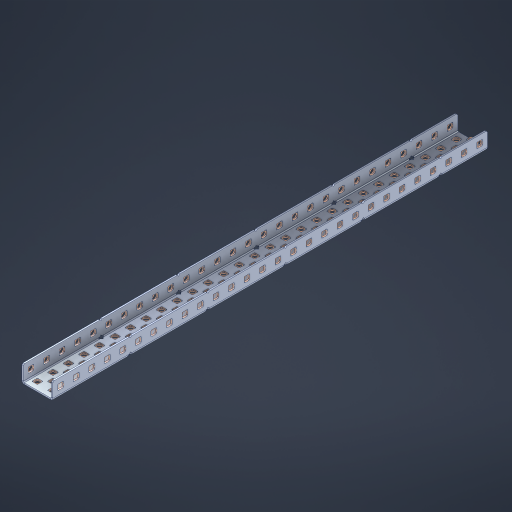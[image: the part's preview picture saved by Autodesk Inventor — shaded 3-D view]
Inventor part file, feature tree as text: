
AUTODESK INVENTOR PART (.ipt)
format: ipt  version: 2023 (Build 270158000, 158)  size: 1,764,864 bytes
history: native  units: in
note: dims shown in document units (in); Inventor stores cm internally (conversion verified against a paired STEP export)
features: other x147, extrude x138, sheet_metal_op x11, sketch x10, pattern_linear x2, mirror x1, chamfer x1
ambient origin geometry x8: Origin, YZ Plane, XZ Plane, XY Plane, X Axis, Y Axis, Z Axis, Center Point
bodies: Solid1 (feature_tree), Body (feature_tree)
feature tree (310):
  sheet_metal_op  "Flanges"
  other  "Flange Pattern Plane"
  other  "Flange Pattern Sketch"
  sheet_metal_op  "Flange Pattern"
  sheet_metal_op  "Body Pattern"
  pattern_linear  "Center Pattern"  Spacing1=0.0469in  [1 undecoded]
  other  "Arc Length"
  mirror  "Notch Mirror"
  pattern_linear  "Notch Pattern"  Spacing1=0.182in  [1 undecoded]
  chamfer  "End Chamfer"
  extrude  "Half Cut"  Depth=0.02in
  sketch  "Sketch1"  dims[d0=1.0in]
  other  "Plate1"
  sketch  "Sketch2"  dims[d1=14.0in]
  other  "Plate2"
  sheet_metal_op  "Bend1"
  sheet_metal_op  "Corner1"
  sketch  "Sketch3"  dims[d2=0.0469in]
  sketch  "Sketch7"  dims[d3=0.0469in]
  other  "Srf1"
  other  "Srf2"
  sketch  "Sketch8"  dims[d4=0.0234in]
  sketch  "Sketch9"  dims[d5=0.0938in]
  other  "Srf91"
  sheet_metal_op  "Body Pattern Sketch"
  other  "Srf92"
  sketch  "Sketch13"  dims[d6=0.0469in]
  sketch  "Sketch14"  dims[d7=0.5in d8=90.0deg d9=0.0312in]
  sketch  "Sketch15"  dims[d10=0.1875in]
  sketch  "Sketch16"  dims[d11=0.0469in d12=0.0469in d16=0.182in d17=0.02in d18=0.0469in d19=0.0in d20=0.25in d21=0.25in d38=11.0236in d40=0.5in d41=0.7874in d43=1.0in d46=0.172in d47=1.0in d48=0.0in d49=0.182in d50=0.02in d51=0.25in d52=0.25in d53=0.0469in d54=0.0in d55=0.172in d56=1.0in d57=0.0in d58=0.25in d60=11.0236in d62=0.5in d63=0.7874in d65=0.5in d85=0.1227in d86=0.1659in d88=0.04in d89=0.0469in d90=0.0in d91=0.04in d92=0.0491in d95=2.5in d96=0.04in d97=0.25in d98=45.0deg d99=0.25in d100=0.5in d101=0.0in d102=2.497in d106=0.182in d107=0.02in d108=0.5in d109=0.5in d110=0.0469in d111=0.0in d112=0.172in d113=0.5in d114=0.0in d117=0.5in d118=0.5in d119=0.5in]
  other  "Srf786"
  other  "Srf823"
  other  "Srf824"
  other  "Srf825"
  other  "Srf826"
  other  "Srf827"
  other  "Srf828"
  other  "Srf829"
  other  "Srf856"
  other  "Srf857"
  other  "Srf858"
  other  "Srf859"
  other  "Srf860"
  other  "Srf861"
  other  "Srf862"
  other  "Srf889"
  other  "Srf890"
  other  "Srf891"
  other  "Srf892"
  other  "Srf893"
  other  "Srf894"
  other  "Srf895"
  other  "Srf896"
  other  "Srf922"
  other  "Srf923"
  other  "Srf924"
  other  "Srf925"
  other  "Srf926"
  other  "Srf959"
  other  "Srf960"
  other  "Srf961"
  other  "Srf962"
  other  "Srf963"
  other  "Srf996"
  other  "Srf997"
  other  "Srf998"
  other  "Srf999"
  other  "Srf1000"
  other  "Srf1143"
  other  "Srf1144"
  other  "Srf1145"
  other  "Srf1146"
  other  "Srf1147"
  other  "Srf1148"
  other  "Srf1149"
  other  "Srf1150"
  other  "Srf1151"
  other  "Srf1152"
  other  "Srf1153"
  other  "Srf1154"
  other  "Srf1155"
  other  "Srf1156"
  other  "Srf1157"
  other  "Srf1158"
  other  "Srf1159"
  other  "Srf1160"
  other  "Srf1161"
  other  "Srf1162"
  other  "Srf1163"
  other  "Srf1164"
  other  "Srf1165"
  other  "Srf1166"
  other  "Srf1167"
  other  "Srf1168"
  other  "Srf1169"
  other  "Srf1170"
  other  "Srf1171"
  other  "Srf1172"
  other  "Srf1173"
  other  "Srf1174"
  other  "Srf1175"
  other  "Srf1176"
  other  "Srf1177"
  other  "Srf1178"
  other  "Srf1179"
  other  "Srf1180"
  other  "Srf1181"
  other  "Srf1182"
  other  "Srf1183"
  other  "Srf1184"
  other  "Srf1199"
  other  "Srf1200"
  other  "Srf1201"
  other  "Srf1202"
  other  "Srf1203"
  other  "Srf1204"
  other  "Srf1205"
  other  "Srf1206"
  other  "Srf1207"
  other  "Srf1208"
  other  "Srf1209"
  other  "Srf1210"
  other  "Srf1211"
  other  "Srf1212"
  other  "Srf1213"
  other  "Srf1214"
  other  "Srf1215"
  other  "Srf1216"
  other  "Srf1217"
  other  "Srf1218"
  other  "Srf1219"
  other  "Srf1220"
  other  "Srf1221"
  other  "Srf1222"
  other  "Srf1223"
  other  "Srf1224"
  other  "Srf1225"
  other  "Srf1226"
  other  "Srf1227"
  other  "Srf1228"
  other  "Srf1229"
  other  "Srf1230"
  other  "Srf1231"
  other  "Srf1232"
  other  "Srf1233"
  other  "Srf1234"
  other  "Srf1235"
  other  "Srf1236"
  other  "Srf1237"
  other  "Srf1238"
  other  "Srf1239"
  other  "Srf1240"
  other  "Srf1255"
  other  "Srf1256"
  other  "Srf1257"
  other  "Srf1258"
  other  "Srf1259"
  other  "Srf1260"
  other  "Srf1261"
  other  "Srf1262"
  other  "Srf1263"
  other  "Srf1264"
  other  "Srf1265"
  other  "Srf1266"
  other  "Srf1267"
  other  "Srf1268"
  sheet_metal_op  "Flange Stamp"
  sheet_metal_op  "Flange Circle"
  sheet_metal_op  "Body Stamp"
  sheet_metal_op  "Body Circle"
  other  "Center Stamp"
  other  "Center Circle"
  sheet_metal_op  "Notch"
  extrude  "ExtrusionSrf2"  Depth=0.0469in
  extrude  "ExtrusionSrf92"  TaperAngle=0.0deg  [1 undecoded]
  extrude  "ExtrusionSrf823"  Depth=0.5in
  extrude  "ExtrusionSrf824"  Depth=0.5in
  extrude  "ExtrusionSrf825"  Depth=0.5in
  extrude  "ExtrusionSrf826"  Depth=0.5in
  extrude  "ExtrusionSrf827"  Depth=1.0in TaperAngle=0.0deg
  extrude  "ExtrusionSrf828"  Depth=0.5in
  extrude  "ExtrusionSrf829"  Depth=0.02in
  extrude  "ExtrusionSrf856"  Depth=0.5in
  extrude  "ExtrusionSrf857"  Depth=0.5in
  extrude  "ExtrusionSrf858"  Depth=0.0469in
  extrude  "ExtrusionSrf859"  TaperAngle=0.0deg  [1 undecoded]
  extrude  "ExtrusionSrf860"  Depth=0.5in
  extrude  "ExtrusionSrf861"  Depth=1.0in TaperAngle=0.0deg
  extrude  "ExtrusionSrf862"  Depth=0.5in
  extrude  "ExtrusionSrf889"  Depth=0.5in
  extrude  "ExtrusionSrf890"  Depth=0.5in
  extrude  "ExtrusionSrf891"  Depth=0.5in
  extrude  "ExtrusionSrf892"  Depth=0.5in
  extrude  "ExtrusionSrf893"  Depth=0.5in
  extrude  "ExtrusionSrf894"  Depth=0.0469in
  extrude  "ExtrusionSrf895"  TaperAngle=0.0deg  [1 undecoded]
  extrude  "ExtrusionSrf896"  Depth=0.5in
  extrude  "ExtrusionSrf922"  Depth=0.5in
  extrude  "ExtrusionSrf923"  Depth=2.5in
  extrude  "ExtrusionSrf924"  Depth=0.5in TaperAngle=45.0deg
  extrude  "ExtrusionSrf925"  Depth=0.5in
  extrude  "ExtrusionSrf926"  Depth=0.5in TaperAngle=0.0deg
  extrude  "ExtrusionSrf959"  Depth=0.5in
  extrude  "ExtrusionSrf960"  Depth=0.5in
  extrude  "ExtrusionSrf961"  Depth=0.02in
  extrude  "ExtrusionSrf962"  Depth=0.5in
  extrude  "ExtrusionSrf963"  Depth=0.5in
  extrude  "ExtrusionSrf996"  Depth=0.0469in
  extrude  "ExtrusionSrf997"  TaperAngle=0.0deg  [1 undecoded]
  extrude  "ExtrusionSrf998"  Depth=0.5in
  extrude  "ExtrusionSrf999"  Depth=0.5in TaperAngle=0.0deg
  extrude  "ExtrusionSrf1000"  Depth=0.5in
  extrude  "ExtrusionSrf1143"  Depth=0.5in
  extrude  "ExtrusionSrf1144"  Depth=0.5in
  extrude  "ExtrusionSrf1145"  [1 undecoded]
  extrude  "ExtrusionSrf1146"  [1 undecoded]
  extrude  "ExtrusionSrf1147"  [1 undecoded]
  extrude  "ExtrusionSrf1148"  [1 undecoded]
  extrude  "ExtrusionSrf1149"  [1 undecoded]
  extrude  "ExtrusionSrf1150"  [1 undecoded]
  extrude  "ExtrusionSrf1151"  [1 undecoded]
  extrude  "ExtrusionSrf1152"  [1 undecoded]
  extrude  "ExtrusionSrf1153"  [1 undecoded]
  extrude  "ExtrusionSrf1154"  [1 undecoded]
  extrude  "ExtrusionSrf1155"  [1 undecoded]
  extrude  "ExtrusionSrf1156"  [1 undecoded]
  extrude  "ExtrusionSrf1157"  [1 undecoded]
  extrude  "ExtrusionSrf1158"  [1 undecoded]
  extrude  "ExtrusionSrf1159"  [1 undecoded]
  extrude  "ExtrusionSrf1160"  [1 undecoded]
  extrude  "ExtrusionSrf1161"  [1 undecoded]
  extrude  "ExtrusionSrf1162"  [1 undecoded]
  extrude  "ExtrusionSrf1163"  [1 undecoded]
  extrude  "ExtrusionSrf1164"  [1 undecoded]
  extrude  "ExtrusionSrf1165"  [1 undecoded]
  extrude  "ExtrusionSrf1166"  [1 undecoded]
  extrude  "ExtrusionSrf1167"  [1 undecoded]
  extrude  "ExtrusionSrf1168"  [1 undecoded]
  extrude  "ExtrusionSrf1169"  [1 undecoded]
  extrude  "ExtrusionSrf1170"  [1 undecoded]
  extrude  "ExtrusionSrf1171"  [1 undecoded]
  extrude  "ExtrusionSrf1172"  [1 undecoded]
  extrude  "ExtrusionSrf1173"  [1 undecoded]
  extrude  "ExtrusionSrf1174"  [1 undecoded]
  extrude  "ExtrusionSrf1175"  [1 undecoded]
  extrude  "ExtrusionSrf1176"  [1 undecoded]
  extrude  "ExtrusionSrf1177"  [1 undecoded]
  extrude  "ExtrusionSrf1178"  [1 undecoded]
  extrude  "ExtrusionSrf1179"  [1 undecoded]
  extrude  "ExtrusionSrf1180"  [1 undecoded]
  extrude  "ExtrusionSrf1181"  [1 undecoded]
  extrude  "ExtrusionSrf1182"  [1 undecoded]
  extrude  "ExtrusionSrf1183"  [1 undecoded]
  extrude  "ExtrusionSrf1184"  [1 undecoded]
  extrude  "ExtrusionSrf1199"  [1 undecoded]
  extrude  "ExtrusionSrf1200"  [1 undecoded]
  extrude  "ExtrusionSrf1201"  [1 undecoded]
  extrude  "ExtrusionSrf1202"  [1 undecoded]
  extrude  "ExtrusionSrf1203"  [1 undecoded]
  extrude  "ExtrusionSrf1204"  [1 undecoded]
  extrude  "ExtrusionSrf1205"  [1 undecoded]
  extrude  "ExtrusionSrf1206"  [1 undecoded]
  extrude  "ExtrusionSrf1207"  [1 undecoded]
  extrude  "ExtrusionSrf1208"  [1 undecoded]
  extrude  "ExtrusionSrf1209"  [1 undecoded]
  extrude  "ExtrusionSrf1210"  [1 undecoded]
  extrude  "ExtrusionSrf1211"  [1 undecoded]
  extrude  "ExtrusionSrf1212"  [1 undecoded]
  extrude  "ExtrusionSrf1213"  [1 undecoded]
  extrude  "ExtrusionSrf1214"  [1 undecoded]
  extrude  "ExtrusionSrf1215"  [1 undecoded]
  extrude  "ExtrusionSrf1216"  [1 undecoded]
  extrude  "ExtrusionSrf1217"  [1 undecoded]
  extrude  "ExtrusionSrf1218"  [1 undecoded]
  extrude  "ExtrusionSrf1219"  [1 undecoded]
  extrude  "ExtrusionSrf1220"  [1 undecoded]
  extrude  "ExtrusionSrf1221"  [1 undecoded]
  extrude  "ExtrusionSrf1222"  [1 undecoded]
  extrude  "ExtrusionSrf1223"  [1 undecoded]
  extrude  "ExtrusionSrf1224"  [1 undecoded]
  extrude  "ExtrusionSrf1225"  [1 undecoded]
  extrude  "ExtrusionSrf1226"  [1 undecoded]
  extrude  "ExtrusionSrf1227"  [1 undecoded]
  extrude  "ExtrusionSrf1228"  [1 undecoded]
  extrude  "ExtrusionSrf1229"  [1 undecoded]
  extrude  "ExtrusionSrf1230"  [1 undecoded]
  extrude  "ExtrusionSrf1231"  [1 undecoded]
  extrude  "ExtrusionSrf1232"  [1 undecoded]
  extrude  "ExtrusionSrf1233"  [1 undecoded]
  extrude  "ExtrusionSrf1234"  [1 undecoded]
  extrude  "ExtrusionSrf1235"  [1 undecoded]
  extrude  "ExtrusionSrf1236"  [1 undecoded]
  extrude  "ExtrusionSrf1237"  [1 undecoded]
  extrude  "ExtrusionSrf1238"  [1 undecoded]
  extrude  "ExtrusionSrf1239"  [1 undecoded]
  extrude  "ExtrusionSrf1240"  [1 undecoded]
  extrude  "ExtrusionSrf1255"  [1 undecoded]
  extrude  "ExtrusionSrf1256"  [1 undecoded]
  extrude  "ExtrusionSrf1257"  [1 undecoded]
  extrude  "ExtrusionSrf1258"  [1 undecoded]
  extrude  "ExtrusionSrf1259"  [1 undecoded]
  extrude  "ExtrusionSrf1260"  [1 undecoded]
  extrude  "ExtrusionSrf1261"  [1 undecoded]
  extrude  "ExtrusionSrf1262"  [1 undecoded]
  extrude  "ExtrusionSrf1263"  [1 undecoded]
  extrude  "ExtrusionSrf1264"  [1 undecoded]
  extrude  "ExtrusionSrf1265"  [1 undecoded]
  extrude  "ExtrusionSrf1266"  [1 undecoded]
  extrude  "ExtrusionSrf1267"  [1 undecoded]
  extrude  "ExtrusionSrf1268"  [1 undecoded]
note: 102 required parameter values undecoded (feature->parameter linkage not recoverable at this tier; creation-order binding heuristic only, values carry confidence <= 0.55)
